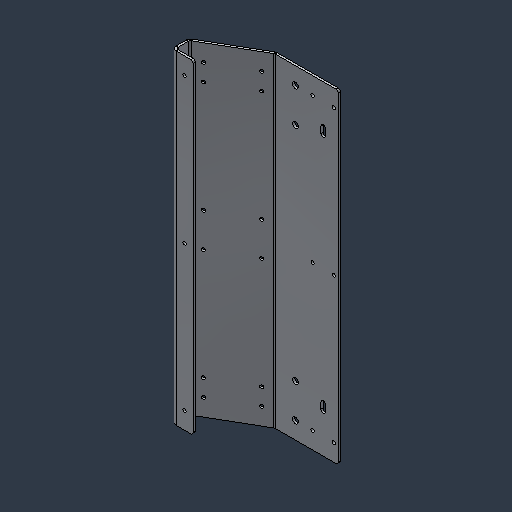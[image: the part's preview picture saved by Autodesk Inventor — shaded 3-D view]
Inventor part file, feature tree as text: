
AUTODESK INVENTOR PART (.ipt)
format: ipt  version: 2024.3 (Build 283343000, 343)  size: 137,216 bytes
history: native  units: mm (DEFAULTED — no unit token found)
features: fillet x1
ambient origin geometry x8: Origin, YZ Plane, XZ Plane, XY Plane, X Axis, Y Axis, Z Axis, Center Point
bodies: Solid1 (feature_tree)
feature tree (1):
  fillet  "Fillet1"  [1 undecoded]
note: 1 required parameter value undecoded (feature->parameter linkage not recoverable at this tier; creation-order binding heuristic only, values carry confidence <= 0.55)
